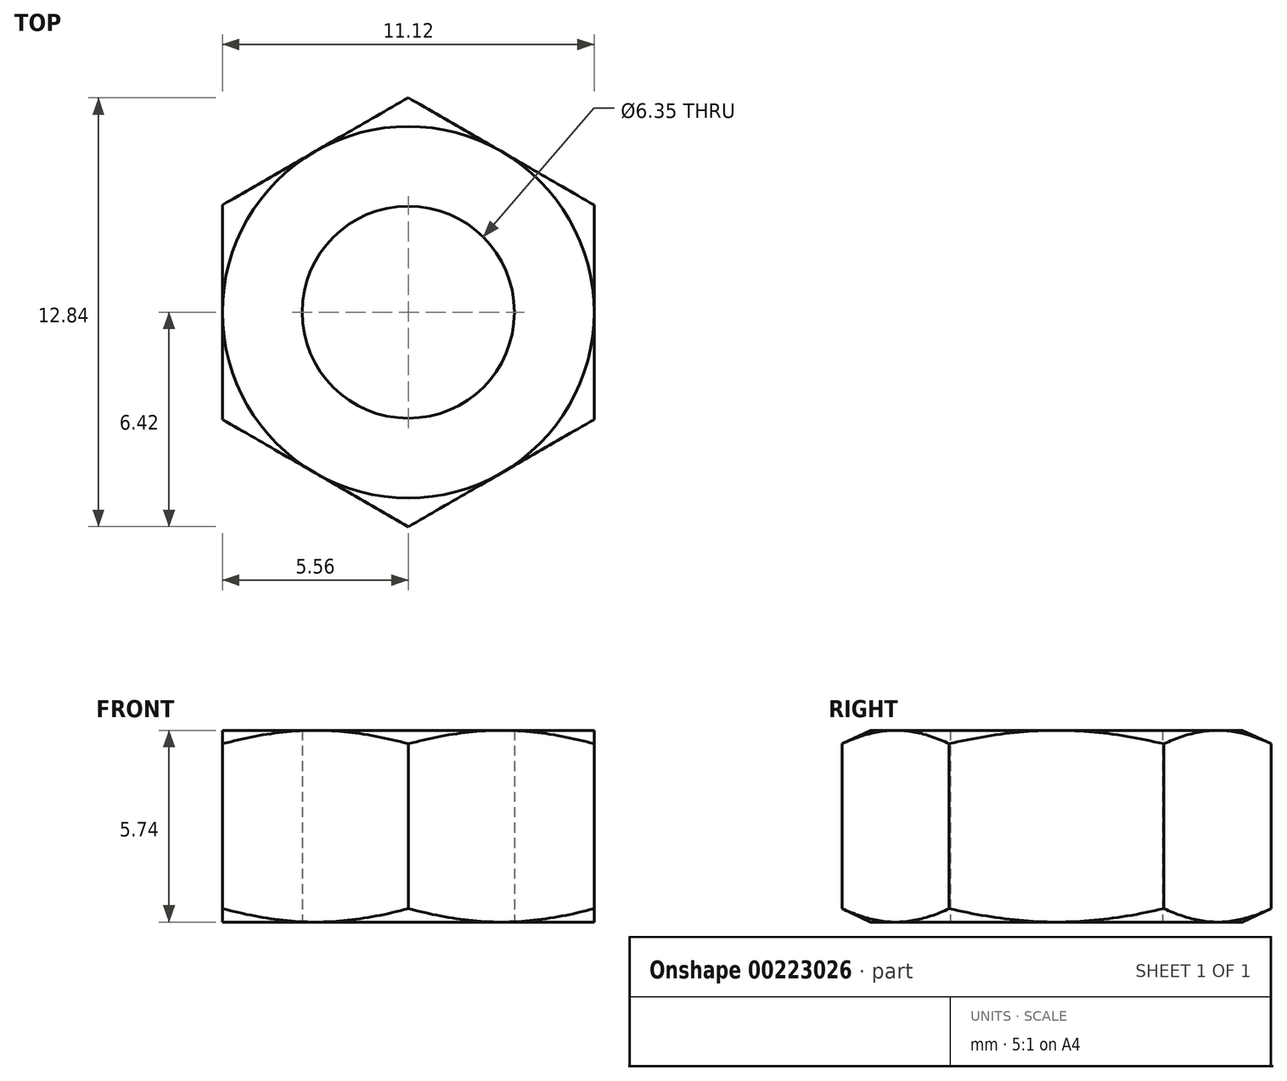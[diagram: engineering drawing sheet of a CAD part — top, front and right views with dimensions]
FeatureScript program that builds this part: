
annotation { "Feature Type Name" : "Feature", "Feature Type Description" : "" }
export const myFeature = defineFeature(function(context is Context, id is Id, definition is map)
    precondition{}
    {
        {
            var Q0;
            Q0=qCreatedBy(makeId("Top.planeOp"),FACE);
            var sketch = newSketch(context, id + "F0", { "sketchPlane" : qUnion([Q0])});
            skCircle(sketch, "E0.cCircle", {"center": v(0, 0) * mm, "radius": 5.56 * mm, "construction": true});
            skLineSegment(sketch, "E0.0", {"start": v(5.56, -3.21) * mm, "end": v(0, -6.42) * mm});
            skLineSegment(sketch, "E0.1", {"start": v(0, -6.42) * mm, "end": v(-5.56, -3.21) * mm});
            skLineSegment(sketch, "E0.2", {"start": v(-5.56, -3.21) * mm, "end": v(-5.56, 3.21) * mm});
            skLineSegment(sketch, "E0.3", {"start": v(-5.56, 3.21) * mm, "end": v(0, 6.42) * mm});
            skLineSegment(sketch, "E0.4", {"start": v(0, 6.42) * mm, "end": v(5.56, 3.21) * mm});
            skLineSegment(sketch, "E0.5", {"start": v(5.56, 3.21) * mm, "end": v(5.56, -3.21) * mm});
            skPoint(sketch, "E0.0.midPoint", {"position": v(2.78, -4.82) * mm});
            skCircle(sketch, "E1", {"center": v(0, 0) * mm, "radius": 3.18 * mm});
            skSolve(sketch);
        }
        {
            var Q0;
            Q0=makeQuery(id+"F0.imprint","IMPRINT",FACE,{"disambiguationData":[TD([[makeQuery(id+"F0.imprint","IMPRINT",EDGE,{"derivedFrom":sQuery(id+"F0.wireOp",EDGE,"E0.0")}),-1.0]])]});
            extrude(context, id + "F1", {"entities" : qUnion([Q0]), "endBound" : BoundingType.SYMMETRIC, "depth" : 5.74 * mm});
        }
        {
            var Q0;
            Q0=qCreatedBy(makeId("Front.planeOp"),FACE);
            var sketch = newSketch(context, id + "F2", { "sketchPlane" : qUnion([Q0])});
            skPoint(sketch, "E2.0", {"position": v(5.56, 2.87) * mm});
            skLineSegment(sketch, "E3", {"start": v(5.56, 2.87) * mm, "end": v(6.77, 2.3) * mm});
            skLineSegment(sketch, "E4", {"start": v(6.77, 2.3) * mm, "end": v(6.77, 2.87) * mm});
            skLineSegment(sketch, "E5", {"start": v(6.77, 2.87) * mm, "end": v(5.56, 2.87) * mm});
            skLineSegment(sketch, "E6", {"start": v(-7.67, 0) * mm, "end": v(8.24, 0) * mm, "construction": true});
            skPoint(sketch, "E7.MirrorP", {"position": v(5.56, -2.87) * mm});
            skLineSegment(sketch, "E8.MirrorCS", {"start": v(6.77, -2.3) * mm, "end": v(6.77, -2.87) * mm});
            skLineSegment(sketch, "E9.MirrorCS", {"start": v(6.77, -2.87) * mm, "end": v(5.56, -2.87) * mm});
            skLineSegment(sketch, "E10.MirrorCS", {"start": v(5.56, -2.87) * mm, "end": v(6.77, -2.3) * mm});
            skSolve(sketch);
        }
        {
            var Q0;
            Q0=makeQuery(id+"F2.imprint","IMPRINT",FACE,{"disambiguationData":[TD([[makeQuery(id+"F2.imprint","IMPRINT",EDGE,{"derivedFrom":sQuery(id+"F2.wireOp",EDGE,"E3")}),1.0]])]});
            var Q1;
            Q1=makeQuery(id+"F1.opExtrude","CAP_EDGE",EDGE,{"disambiguationData":[OSD([sQuery(id+"F0.wireOp",EDGE,"E1")])],"isStart":false});
            revolve(context, id + "F3", {"operationType" : NewBodyOperationType.REMOVE, "entities" : qUnion([Q0]), "axis" : qUnion([Q1]), "revolveType" : RevolveType.FULL, "oppositeDirection" : true});
        }
        {
            var Q0;
            Q0=makeQuery(id+"F2.imprint","IMPRINT",FACE,{"disambiguationData":[TD([[makeQuery(id+"F2.imprint","IMPRINT",EDGE,{"derivedFrom":sQuery(id+"F2.wireOp",EDGE,"E8.MirrorCS")}),-1.0]])]});
            var Q1;
            Q1=makeQuery(id+"F1.opExtrude","CAP_EDGE",EDGE,{"disambiguationData":[OSD([sQuery(id+"F0.wireOp",EDGE,"E1")])],"isStart":true});
            revolve(context, id + "F4", {"operationType" : NewBodyOperationType.REMOVE, "entities" : qUnion([Q0]), "axis" : qUnion([Q1]), "revolveType" : RevolveType.FULL, "oppositeDirection" : true});
        }
    });
